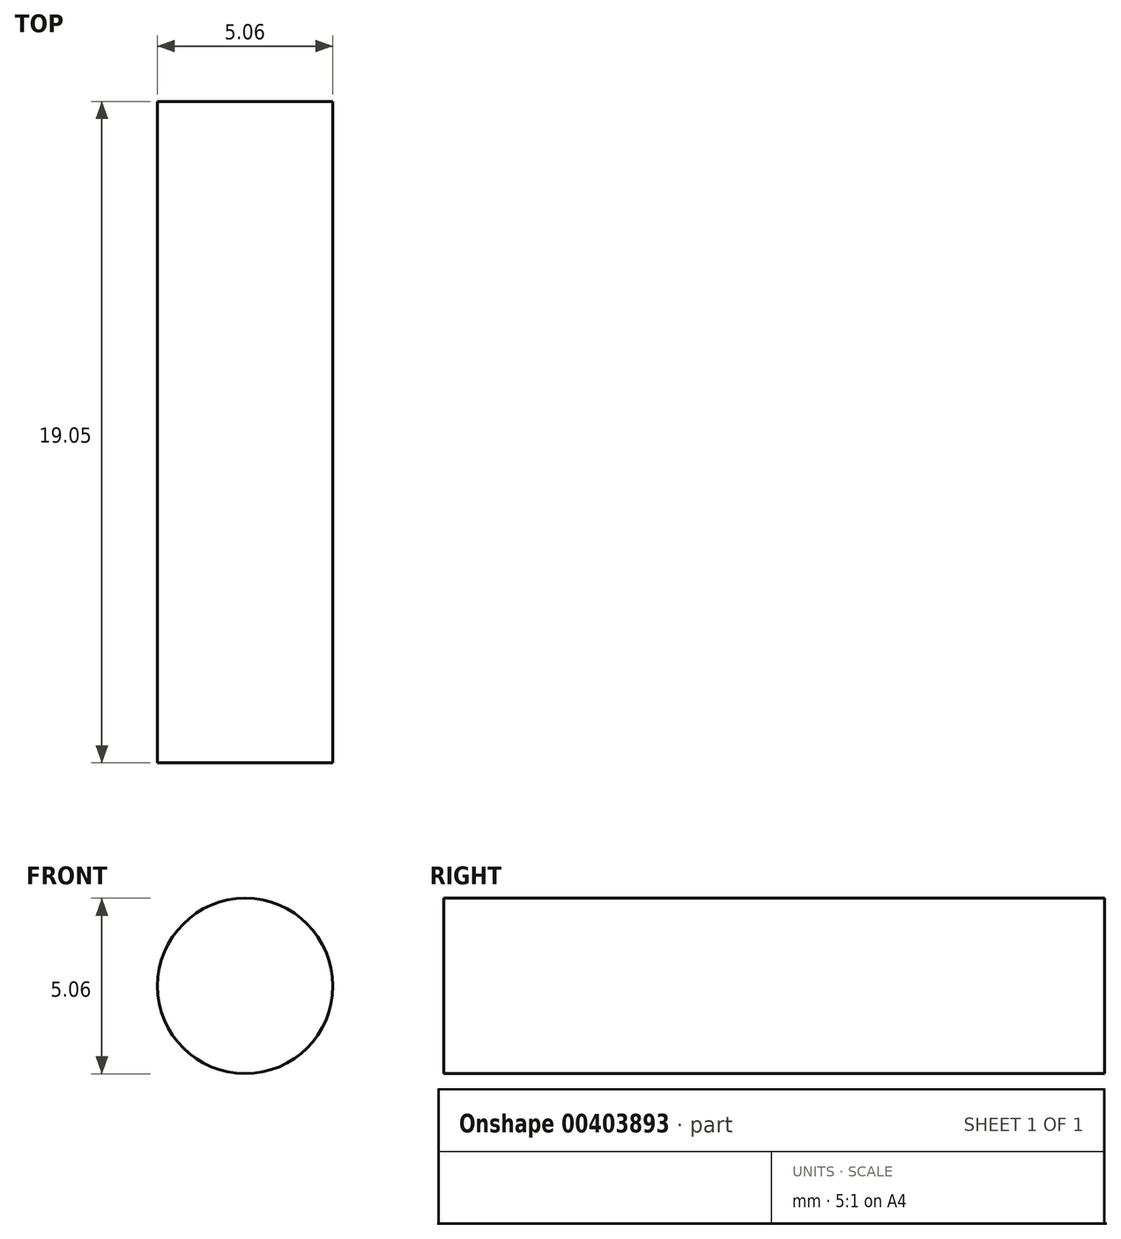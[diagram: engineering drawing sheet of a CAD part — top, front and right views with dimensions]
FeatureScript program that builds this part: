
annotation { "Feature Type Name" : "Feature", "Feature Type Description" : "" }
export const myFeature = defineFeature(function(context is Context, id is Id, definition is map)
    precondition{}
    {
        {
            var Q0;
            Q0=qCreatedBy(makeId("Front.planeOp"),FACE);
            var sketch = newSketch(context, id + "F0", { "sketchPlane" : qUnion([Q0])});
            skCircle(sketch, "E0", {"center": v(0, 0) * mm, "radius": 2.53 * mm});
            skSolve(sketch);
        }
        {
            var Q0;
            Q0=qSketchRegion(id+"F0",true);
            extrude(context, id + "F1", {"entities" : qUnion([Q0]), "depth" : 19.05 * mm});
        }
    });
